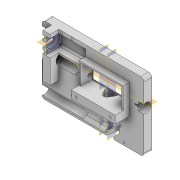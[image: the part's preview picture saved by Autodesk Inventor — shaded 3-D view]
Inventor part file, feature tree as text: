
AUTODESK INVENTOR PART (.ipt)
format: ipt  version: 2022 (Build 260153000, 153)  size: 643,584 bytes
history: native  units: mm
features: sketch x27, extrude x26, projected_geometry x14, reference x8, other x6, plane x5, fillet x4, chamfer x1, mirror x1, hole x1
ambient origin geometry x8: Origin, YZ Plane, XZ Plane, XY Plane, X Axis, Y Axis, Z Axis, Center Point
bodies: Solid1 (feature_tree)
feature tree (93):
  extrude  "Extrusion1"  Depth=85.5mm
  fillet  "Fillet1"  Radius=10.0mm
  extrude  "Extrusion2"  Depth=4.0mm
  extrude  "Extrusion3"  Depth=20.0mm
  plane  "Work Plane1"
  plane  "Work Plane2"
  chamfer  "Chamfer1"  [1 undecoded]
  extrude  "Extrusion4"  Depth=10.0mm
  extrude  "Extrusion5"  Depth=1.9mm
  extrude  "Extrusion6"  Depth=4.0mm TaperAngle=0.0deg
  extrude  "Extrusion7"  Depth=18.0mm TaperAngle=0.0deg
  extrude  "Extrusion8"  Depth=2.1mm
  plane  "Work Plane3"
  extrude  "Extrusion9"  Depth=6.0mm TaperAngle=0.0deg
  extrude  "Extrusion10"  Depth=10.0mm TaperAngle=0.0deg
  fillet  "Fillet3"  Radius=10.0mm
  extrude  "Extrusion11"  Depth=10.0mm
  extrude  "Extrusion12"  Depth=4.0mm
  extrude  "Extrusion13"  Depth=2.8mm
  mirror  "Mirror1"
  plane  "Work Plane4"
  extrude  "Extrusion14"  Depth=2.0mm
  sketch  "Sketch15"  dims[d39=20.0mm d40=10.0mm d41=0.0mm d42=0.0mm d44=12.2mm]
  plane  "Work Plane5"
  extrude  "Extrusion15"  Depth=2.0mm
  extrude  "Extrusion16"  Depth=12.0mm
  hole  "Hole1"  [1 undecoded]
  extrude  "Extrusion17"  Depth=2.8mm
  extrude  "Extrusion18"  Depth=12.0mm
  extrude  "Extrusion19"  Depth=0.5mm
  extrude  "Extrusion20"  Depth=4.0mm
  extrude  "Extrusion21"  Depth=10.0mm TaperAngle=0.0deg
  fillet  "Fillet4"  Radius=19.0mm
  extrude  "Extrusion22"  Depth=2.0mm
  extrude  "Extrusion23"  Depth=10.0mm TaperAngle=0.0deg
  extrude  "Extrusion24"  Depth=2.0mm
  fillet  "Fillet5"  Radius=12.9mm
  extrude  "Extrusion25"  Depth=2.0mm TaperAngle=0.0deg
  extrude  "Extrusion26"  Depth=2.0mm
  sketch  "Sketch1"  dims[d0=127.8mm d1=85.5mm d2=10.0mm d3=0.0mm]
  sketch  "Sketch2"  dims[d4=4.0mm d5=51.0mm]
  projected_geometry  "Projected Loop1"
  sketch  "Sketch3"  dims[d6=25.0mm d7=20.0mm]
  projected_geometry  "Projected Loop2"
  sketch  "Sketch4"  dims[d8=15.0mm]
  projected_geometry  "Projected Loop3"
  sketch  "Sketch5"  dims[d9=6.0mm]
  sketch  "Sketch6"  dims[d10=0.0mm]
  reference  "Reference2"
  sketch  "Sketch7"  dims[d11=1.5mm d12=0.0mm d13=0.0mm]
  sketch  "Sketch8"  dims[d14=4.0mm d15=2.0mm d16=45.0deg d17=10.0mm]
  reference  "Reference3"
  sketch  "Sketch9"  dims[d18=8.0mm d19=0.0mm d20=1.9mm]
  projected_geometry  "Projected Loop4"
  sketch  "Sketch10"  dims[d21=4.0mm d22=5.0mm d23=0.0mm]
  sketch  "Sketch11"  dims[d27=20.0mm d28=18.0mm d29=0.0mm]
  projected_geometry  "Projected Loop5"
  sketch  "Sketch12"  dims[d30=45.0deg d31=2.1mm]
  reference  "Reference4"
  sketch  "Sketch13"  dims[d32=7.0mm d33=6.0mm d34=0.0mm]
  sketch  "Sketch14"  dims[d35=6.0mm d36=8.0mm d37=0.0mm d38=10.0mm]
  reference  "Reference5"
  projected_geometry  "Projected Loop6"
  sketch  "Sketch16"  dims[d45=0.0mm d46=0.0mm d47=4.0mm]
  reference  "Reference6"
  sketch  "Sketch17"  dims[d48=2.8mm d49=2.8mm]
  reference  "Reference7"
  sketch  "Sketch18"  dims[d50=0.0mm d51=0.0mm d52=2.0mm]
  sketch  "Sketch19"  dims[d53=2.0mm d54=2.0mm]
  reference  "Reference10"
  sketch  "Sketch20"  dims[d55=32.0mm d56=12.0mm]
  sketch  "Sketch21"  dims[d57=2.8mm d58=2.8mm]
  projected_geometry  "Projected Loop7"
  sketch  "Sketch22"  dims[d59=2.8mm d60=2.8mm]
  projected_geometry  "Projected Loop8"
  sketch  "Sketch23"  dims[d61=30.0mm d62=-0.523599mm d63=12.0mm]
  projected_geometry  "Projected Loop9"
  reference  "Reference11"
  sketch  "Sketch24"  dims[d64=7.0mm d65=0.0mm d66=0.5mm]
  projected_geometry  "Projected Loop10"
  projected_geometry  "Projected Loop11"
  sketch  "Sketch25"  dims[d67=40.0mm d68=0.0mm d69=4.0mm]
  sketch  "Sketch26"  dims[d70=10.0mm d71=0.0mm d72=50.0mm d73=0.0mm]
  projected_geometry  "Projected Loop12"
  sketch  "Sketch27"  dims[d74=2.5mm d75=6.0mm d76=5.0mm d77=14.0mm d78=90.0deg d79=30.0mm d80=20.594885mm d81=19.0mm d82=16.0mm d83=10.0mm d84=0.0mm d85=9.0mm d86=12.9mm d87=30.0mm d88=0.0mm d89=30.0mm d90=30.0mm d91=0.0mm d92=2.0mm d93=0.0mm d94=1.0mm d95=0.0mm d96=2.8mm d97=2.8mm d98=2.8mm d99=2.8mm d100=7.0mm d101=10.0mm d102=0.0mm d103=11.8mm d104=2.0mm d105=2.8mm d106=2.8mm d107=6.0mm d108=6.0mm d109=0.0mm d110=0.0mm d113=8.0mm d114=0.0mm d115=0.0mm d116=0.0mm d117=17.5mm d118=17.5mm d119=5.922006mm d120=2.961003mm d121=8.726646mm d122=2.0mm d123=18.0mm d124=4.0mm d125=4.0mm d126=8.0mm d127=0.0mm d128=2.0mm d129=45.0deg d130=10.0mm d131=1.8mm d132=1.8mm d133=2.0mm d134=2.0mm d135=0.0mm d136=0.0mm d137=1.8mm d138=1.8mm d139=0.0mm d140=0.0mm]
  projected_geometry  "Projected Loop13"
  projected_geometry  "Projected Loop14"
  other  "<userpath>\Documents\Inventor\Guinardia\INVENTOR\Assembly_Guinardia_V0.iam"
  other  "Assembly_Guinardia_V0.iam"
  other  "00_CCTV_lens_M12_25mm_5mp:1"
  other  "00_PipetteTip200ul-1:2"
  other  "00_NEMA8:1"
  other  "00_PipetteTip200ul-1:3"
note: 2 required parameter values undecoded (feature->parameter linkage not recoverable at this tier; creation-order binding heuristic only, values carry confidence <= 0.55)
